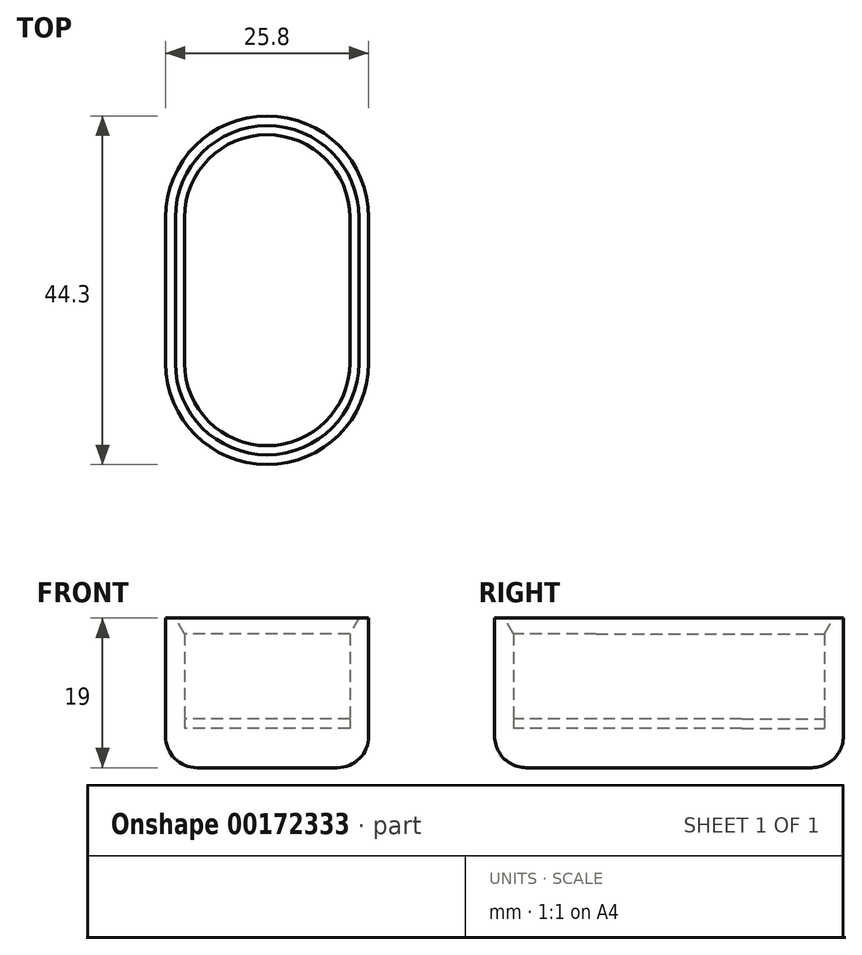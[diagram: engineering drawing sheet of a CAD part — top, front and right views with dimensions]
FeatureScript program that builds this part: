
annotation { "Feature Type Name" : "Feature", "Feature Type Description" : "" }
export const myFeature = defineFeature(function(context is Context, id is Id, definition is map)
    precondition{}
    {
        {
            var Q0;
            Q0=qCreatedBy(makeId("Top.planeOp"),FACE);
            var sketch = newSketch(context, id + "F0", { "sketchPlane" : qUnion([Q0])});
            skLineSegment(sketch, "E0.bottom", {"start": v(-10.5, 9.5) * mm, "end": v(10.5, 9.5) * mm, "construction": true});
            skLineSegment(sketch, "E0.top", {"start": v(-10.5, -9) * mm, "end": v(10.5, -9) * mm, "construction": true});
            skLineSegment(sketch, "E0.left", {"start": v(-10.5, 9.5) * mm, "end": v(-10.5, -9) * mm});
            skLineSegment(sketch, "E0.right", {"start": v(10.5, 9.5) * mm, "end": v(10.5, -9) * mm});
            skArc(sketch, "E1", {"start": v(10.5, 9.5) * mm, "mid": v(0, 20) * mm, "end": v(-10.5, 9.5) * mm});
            skArc(sketch, "E2", {"start": v(-10.5, -9) * mm, "mid": v(0, -19.5) * mm, "end": v(10.5, -9) * mm});
            skLineSegment(sketch, "E3", {"start": v(0, 20) * mm, "end": v(0, -19.5) * mm, "construction": true});
            skLineSegment(sketch, "E4.0", {"start": v(-12.9, 9.5) * mm, "end": v(-12.9, -9) * mm});
            skArc(sketch, "E4.1", {"start": v(12.9, 9.5) * mm, "mid": v(0, 22.4) * mm, "end": v(-12.9, 9.5) * mm});
            skLineSegment(sketch, "E4.2", {"start": v(12.9, 9.5) * mm, "end": v(12.9, -9) * mm});
            skArc(sketch, "E4.3", {"start": v(-12.9, -9) * mm, "mid": v(0, -21.9) * mm, "end": v(12.9, -9) * mm});
            skSolve(sketch);
        }
        {
            var Q0;
            Q0=makeQuery(id+"F0.imprint","IMPRINT",FACE,{"disambiguationData":[TD([[makeQuery(id+"F0.imprint","IMPRINT",EDGE,{"derivedFrom":sQuery(id+"F0.wireOp",EDGE,"E0.left")}),-1.0]])]});
            var Q1;
            Q1=makeQuery(id+"F0.imprint","IMPRINT",FACE,{"disambiguationData":[TD([[makeQuery(id+"F0.imprint","IMPRINT",EDGE,{"derivedFrom":sQuery(id+"F0.wireOp",EDGE,"E0.left")}),1.0]])]});
            extrude(context, id + "F1", {"entities" : qUnion([Q0, Q1]), "oppositeDirection" : true, "depth" : 5 * mm});
        }
        {
            var Q0;
            Q0=makeQuery(id+"F0.imprint","IMPRINT",FACE,{"disambiguationData":[TD([[makeQuery(id+"F0.imprint","IMPRINT",EDGE,{"derivedFrom":sQuery(id+"F0.wireOp",EDGE,"E0.left")}),-1.0]])]});
            extrude(context, id + "F2", {"entities" : qUnion([Q0]), "operationType" : NewBodyOperationType.ADD, "depth" : 14 * mm});
        }
        {
            var Q0;
            Q0=makeQuery(id+"F2.opExtrude","CAP_EDGE",EDGE,{"disambiguationData":[OSD([sQuery(id+"F0.wireOp",EDGE,"E0.left")])],"isStart":false});
            var Q1;
            Q1=makeQuery(id+"F2.opExtrude","CAP_EDGE",EDGE,{"disambiguationData":[OSD([sQuery(id+"F0.wireOp",EDGE,"E1")])],"isStart":false});
            var Q2;
            Q2=makeQuery(id+"F2.opExtrude","CAP_EDGE",EDGE,{"disambiguationData":[OSD([sQuery(id+"F0.wireOp",EDGE,"E0.right")])],"isStart":false});
            var Q3;
            Q3=makeQuery(id+"F2.opExtrude","CAP_EDGE",EDGE,{"disambiguationData":[OSD([sQuery(id+"F0.wireOp",EDGE,"E2")])],"isStart":false});
            chamfer(context, id + "F3", {"entities" : qUnion([Q0, Q1, Q2, Q3]), "chamferType" : ChamferType.OFFSET_ANGLE, "width" : 2 * mm, "oppositeDirection" : false, "angle" : 30 * degree, "tangentPropagation" : true});
        }
        {
            var Q0;
            Q0=makeQuery(id+"F1.opExtrude","CAP_FACE",FACE,{"disambiguationData":[OSD([sQuery(id+"F0.wireOp",EDGE,"E4.0"),sQuery(id+"F0.wireOp",EDGE,"E4.1"),sQuery(id+"F0.wireOp",EDGE,"E4.2"),sQuery(id+"F0.wireOp",EDGE,"E4.3")])],"isStart":false});
            fillet(context, id + "F4", {"entities" : qUnion([Q0]), "radius" : 4 * mm, "tangentPropagation" : true, "allowEdgeOverflow" : false});
        }
        {
            var Q0;
            Q0=makeQuery(id+"F1.opExtrude","CAP_FACE",FACE,{"disambiguationData":[OSD([sQuery(id+"F0.wireOp",EDGE,"E4.0"),sQuery(id+"F0.wireOp",EDGE,"E4.1"),sQuery(id+"F0.wireOp",EDGE,"E4.2"),sQuery(id+"F0.wireOp",EDGE,"E4.3")])],"isStart":true});
            var sketch = newSketch(context, id + "F5", { "sketchPlane" : qUnion([Q0])});
            skArc(sketch, "E5.0.0", {"start": v(10.5, 9.5) * mm, "mid": v(0, 20) * mm, "end": v(-10.5, 9.5) * mm});
            skLineSegment(sketch, "E5.0.1", {"start": v(-10.5, 9.5) * mm, "end": v(-10.5, -9) * mm});
            skArc(sketch, "E5.0.2", {"start": v(-10.5, -9) * mm, "mid": v(0, -19.5) * mm, "end": v(10.5, -9) * mm});
            skLineSegment(sketch, "E5.0.3", {"start": v(10.5, -9) * mm, "end": v(10.5, 9.5) * mm});
            skSolve(sketch);
        }
        {
            var Q0;
            Q0=makeQuery(id+"F5.imprint","IMPRINT",FACE,{"disambiguationData":[TD([[makeQuery(id+"F5.imprint","IMPRINT",EDGE,{"derivedFrom":sQuery(id+"F5.wireOp",EDGE,"E5.0.0")}),1.0]])]});
            extrude(context, id + "F6", {"entities" : qUnion([Q0]), "depth" : 1.2 * mm});
        }
    });
